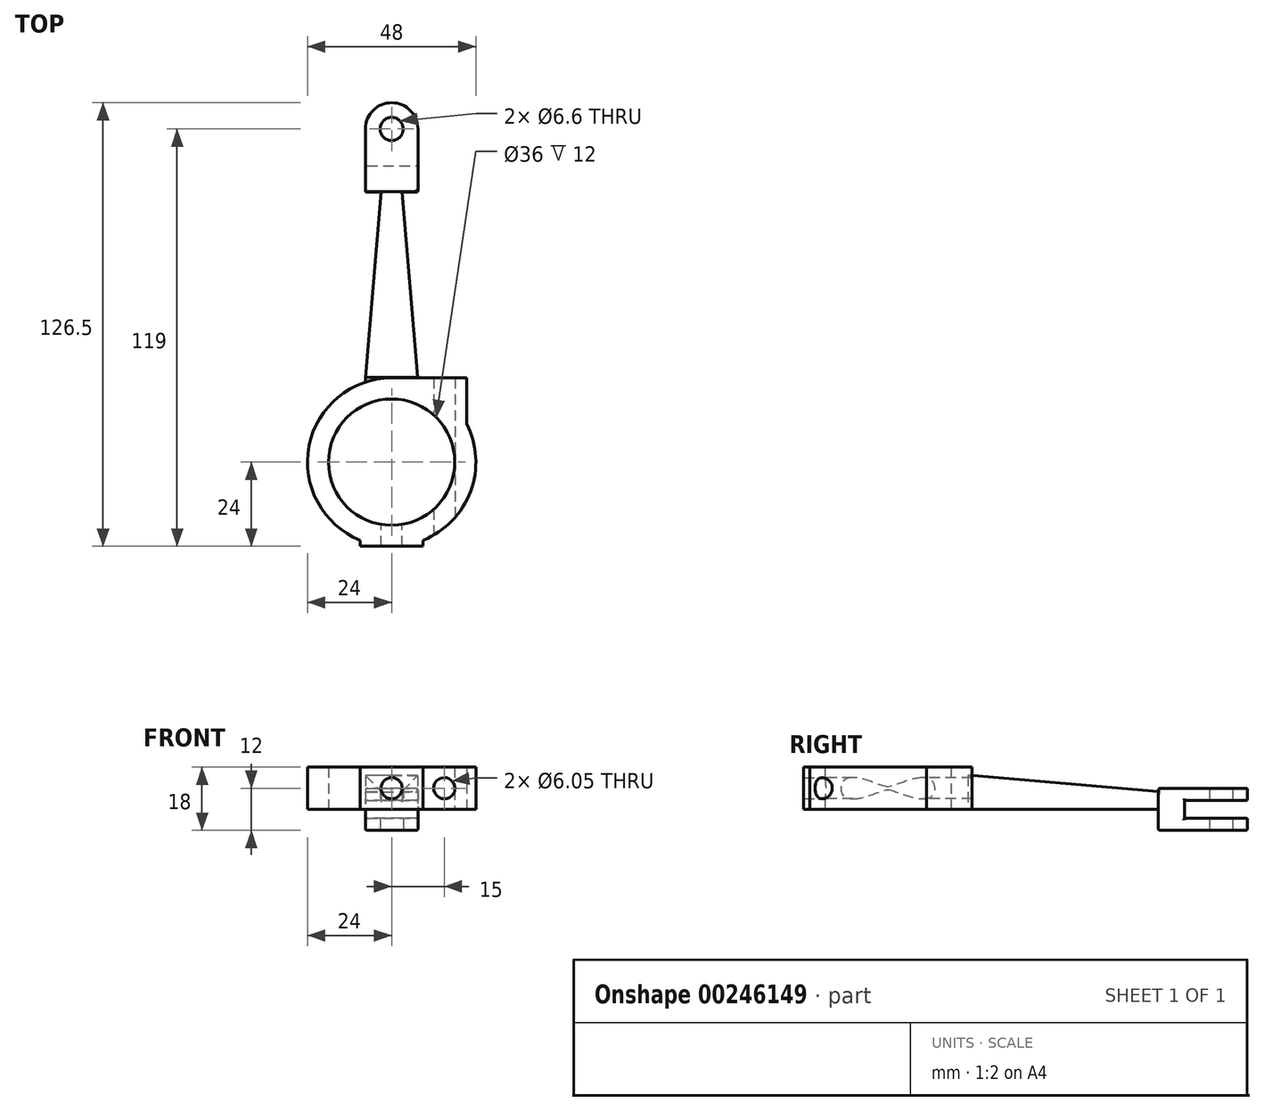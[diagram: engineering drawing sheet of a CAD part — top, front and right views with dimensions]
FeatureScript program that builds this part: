
annotation { "Feature Type Name" : "Feature", "Feature Type Description" : "" }
export const myFeature = defineFeature(function(context is Context, id is Id, definition is map)
    precondition{}
    {
        {
            var Q0;
            Q0=qCreatedBy(makeId("Top.planeOp"),FACE);
            var sketch = newSketch(context, id + "F0", { "sketchPlane" : qUnion([Q0])});
            skCircle(sketch, "E0", {"center": v(0, 0) * mm, "radius": 18 * mm});
            skArc(sketch, "E1", {"start": v(9, -22.25) * mm, "mid": v(22.5, -8.35) * mm, "end": v(21.33, 11) * mm});
            skLineSegment(sketch, "E2", {"start": v(-7.5, 22.8) * mm, "end": v(-3, 77) * mm});
            skLineSegment(sketch, "E3", {"start": v(3, 77) * mm, "end": v(7.4, 24) * mm});
            skLineSegment(sketch, "E4.bottom", {"start": v(-7.5, 95) * mm, "end": v(7.5, 95) * mm, "construction": true});
            skLineSegment(sketch, "E4.left", {"start": v(-7.5, 95) * mm, "end": v(-7.5, 77) * mm});
            skLineSegment(sketch, "E4.right", {"start": v(7.5, 95) * mm, "end": v(7.5, 77) * mm});
            skLineSegment(sketch, "E5", {"start": v(-7.5, 77) * mm, "end": v(-3, 77) * mm});
            skLineSegment(sketch, "E6", {"start": v(3, 77) * mm, "end": v(7.5, 77) * mm});
            skArc(sketch, "E7", {"start": v(7.5, 95) * mm, "mid": v(0, 102.5) * mm, "end": v(-7.5, 95) * mm});
            skCircle(sketch, "E8", {"center": v(0, 95) * mm, "radius": 3.3 * mm});
            skLineSegment(sketch, "E9", {"start": v(0, 24) * mm, "end": v(0, 77) * mm, "construction": true});
            skLineSegment(sketch, "E10", {"start": v(-7.5, 77) * mm, "end": v(7.5, 77) * mm});
            skLineSegment(sketch, "E11", {"start": v(0, 0) * mm, "end": v(0, 95) * mm, "construction": true});
            skLineSegment(sketch, "E12", {"start": v(-9, -22.25) * mm, "end": v(-9, -24) * mm});
            skLineSegment(sketch, "E13", {"start": v(9, -22.25) * mm, "end": v(9, -24) * mm});
            skLineSegment(sketch, "E14", {"start": v(21.33, 11) * mm, "end": v(21.33, 24) * mm});
            skLineSegment(sketch, "E15", {"start": v(21.33, 24) * mm, "end": v(7.4, 24) * mm});
            skLineSegment(sketch, "E16", {"start": v(-9, -24) * mm, "end": v(9, -24) * mm});
            skArc(sketch, "E17.trimOffspring", {"start": v(0, 24) * mm, "mid": v(-23.56, 4.58) * mm, "end": v(-9, -22.25) * mm});
            skLineSegment(sketch, "E18", {"start": v(0, 24) * mm, "end": v(7.4, 24) * mm});
            skSolve(sketch);
        }
        {
            var Q0;
            Q0=makeQuery(id+"F0.imprint","IMPRINT",FACE,{"disambiguationData":[TD([[makeQuery(id+"F0.imprint","IMPRINT",EDGE,{"derivedFrom":sQuery(id+"F0.wireOp",EDGE,"E0")}),-1.0]])]});
            extrude(context, id + "F1", {"entities" : qUnion([Q0]), "depth" : 12 * mm});
        }
        {
            var Q0;
            {var subQ1=sQuery(id+"F0.wireOp",EDGE,"E2");Q0=makeQuery(id+"F0.imprint","IMPRINT",FACE,{"disambiguationData":[TD([[makeQuery(id+"F0.imprint","IMPRINT",EDGE,{"derivedFrom":subQ1}),-1.0]])]});}
            extrude(context, id + "F2", {"entities" : qUnion([Q0]), "operationType" : NewBodyOperationType.ADD, "depth" : 9.6 * mm});
        }
        {
            var Q0;
            {var subQ1=sQuery(id+"F0.wireOp",EDGE,"E4.left");Q0=makeQuery(id+"F0.imprint","IMPRINT",FACE,{"disambiguationData":[TD([[makeQuery(id+"F0.imprint","IMPRINT",EDGE,{"derivedFrom":subQ1}),1.0]])]});}
            extrude(context, id + "F3", {"entities" : qUnion([Q0]), "operationType" : NewBodyOperationType.ADD, "depth" : 6 * mm, "hasSecondDirection" : true, "secondDirectionOppositeDirection" : true, "secondDirectionDepth" : 6 * mm});
        }
        {
            var Q0;
            Q0=qCreatedBy(makeId("Right.planeOp"),FACE);
            var sketch = newSketch(context, id + "F4", { "sketchPlane" : qUnion([Q0])});
            skLineSegment(sketch, "E19", {"start": v(77.12, 5) * mm, "end": v(24.03, 9.61) * mm});
            skLineSegment(sketch, "E20", {"start": v(24.03, 9.61) * mm, "end": v(77.12, 9.61) * mm});
            skLineSegment(sketch, "E21", {"start": v(77.12, 9.61) * mm, "end": v(77.12, 5) * mm});
            skSolve(sketch);
        }
        {
            var Q0;
            Q0 = qSketchRegion(id + "F4", true);
            extrude(context, id + "F5", {"entities" : qUnion([Q0]), "operationType" : NewBodyOperationType.REMOVE, "oppositeDirection" : true, "depth" : 25 * mm, "hasSecondDirection" : true, "secondDirectionOppositeDirection" : false, "secondDirectionDepth" : 25 * mm});
        }
        {
            var Q0;
            Q0=makeQuery(id+"F3.opExtrude","SWEPT_FACE",FACE,{"disambiguationData":[OSD([sQuery(id+"F0.wireOp",EDGE,"E4.right")])]});
            var sketch = newSketch(context, id + "F6", { "sketchPlane" : qUnion([Q0])});
            skLineSegment(sketch, "E22.bottom", {"start": v(102.5, -2.5) * mm, "end": v(84.5, -2.5) * mm});
            skLineSegment(sketch, "E22.top", {"start": v(102.5, 2.5) * mm, "end": v(84.5, 2.5) * mm});
            skLineSegment(sketch, "E22.left", {"start": v(102.5, -2.5) * mm, "end": v(102.5, 2.5) * mm});
            skLineSegment(sketch, "E22.right", {"start": v(84.5, -2.5) * mm, "end": v(84.5, 2.5) * mm});
            skPoint(sketch, "E22.middle", {"position": v(93.5, 0) * mm});
            skSolve(sketch);
        }
        {
            var Q0;
            {var subQ0=sQuery(id+"F6.wireOp",EDGE,"E22.right");Q0=makeQuery(id+"F6.imprint","IMPRINT",FACE,{"disambiguationData":[TD([[makeQuery(id+"F6.imprint","IMPRINT",EDGE,{"derivedFrom":subQ0}),-1.0]])]});}
            var Q1;
            {var subQ0=sQuery(id+"F6.wireOp",EDGE,"E22.left");Q1=makeQuery(id+"F6.imprint","IMPRINT",FACE,{"disambiguationData":[TD([[makeQuery(id+"F6.imprint","IMPRINT",EDGE,{"derivedFrom":subQ0}),1.0]])]});}
            extrude(context, id + "F7", {"entities" : qUnion([Q0, Q1]), "operationType" : NewBodyOperationType.REMOVE, "oppositeDirection" : true, "depth" : 25 * mm});
        }
        {
            var Q0;
            Q0=makeQuery(id+"F1.opExtrude","SWEPT_FACE",FACE,{"disambiguationData":[OSD([sQuery(id+"F0.wireOp",EDGE,"E16")])]});
            var sketch = newSketch(context, id + "F8", { "sketchPlane" : qUnion([Q0])});
            skLineSegment(sketch, "E23", {"start": v(0, 0) * mm, "end": v(0, 12) * mm, "construction": true});
            skLineSegment(sketch, "E24", {"start": v(9, 6) * mm, "end": v(-9, 6) * mm, "construction": true});
            skPoint(sketch, "E25", {"position": v(0, 6) * mm});
            skSolve(sketch);
        }
        {
            var Q0;
            Q0=sQuery(id+"F8.wireOp",VERTEX,"E25");
            var Q1;
            Q1=makeQuery(id+"F1.opExtrude","SWEPT_BODY",BODY,{"disambiguationData":[OSD([sQuery(id+"F0.wireOp",EDGE,"E0"),sQuery(id+"F0.wireOp",EDGE,"E1"),sQuery(id+"F0.wireOp",EDGE,"E12"),sQuery(id+"F0.wireOp",EDGE,"E13"),sQuery(id+"F0.wireOp",EDGE,"E14"),sQuery(id+"F0.wireOp",EDGE,"E15"),sQuery(id+"F0.wireOp",EDGE,"E16"),sQuery(id+"F0.wireOp",EDGE,"E17.trimOffspring"),sQuery(id+"F0.wireOp",EDGE,"E18")])]});
            hole(context, id + "F9", {"style" : HoleStyle.SIMPLE, "endStyle" : HoleEndStyle.BLIND, "holeDiameter" : 5 * mm, "holeDepth" : 17 * mm, "tappedDepth" : 12.7 * mm, "tapClearance" : 3, "locations" : qUnion([Q0]), "scope" : qUnion([Q1]), "startStyle" : HoleStartStyle.PART});
        }
        {
            var Q0;
            Q0=makeQuery(id+"F1.opExtrude","SWEPT_FACE",FACE,{"disambiguationData":[OSD([sQuery(id+"F0.wireOp",EDGE,"E15"),sQuery(id+"F0.wireOp",EDGE,"E18")])]});
            var sketch = newSketch(context, id + "F10", { "sketchPlane" : qUnion([Q0])});
            skLineSegment(sketch, "E26", {"start": v(-21.33, 6) * mm, "end": v(0, 6) * mm, "construction": true});
            skLineSegment(sketch, "E27", {"start": v(-15, 21.84) * mm, "end": v(-15, -13.14) * mm, "construction": true});
            skPoint(sketch, "E28", {"position": v(-15, 6) * mm});
            skSolve(sketch);
        }
        {
            var Q0;
            Q0=sQuery(id+"F10.wireOp",VERTEX,"E28");
            var Q1;
            Q1=makeQuery(id+"F1.opExtrude","SWEPT_BODY",BODY,{"disambiguationData":[OSD([sQuery(id+"F0.wireOp",EDGE,"E0"),sQuery(id+"F0.wireOp",EDGE,"E1"),sQuery(id+"F0.wireOp",EDGE,"E12"),sQuery(id+"F0.wireOp",EDGE,"E13"),sQuery(id+"F0.wireOp",EDGE,"E14"),sQuery(id+"F0.wireOp",EDGE,"E15"),sQuery(id+"F0.wireOp",EDGE,"E16"),sQuery(id+"F0.wireOp",EDGE,"E17.trimOffspring"),sQuery(id+"F0.wireOp",EDGE,"E18")])]});
            hole(context, id + "F11", {"style" : HoleStyle.SIMPLE, "endStyle" : HoleEndStyle.BLIND, "holeDiameter" : 5 * mm, "holeDepth" : 17 * mm, "tappedDepth" : 12.7 * mm, "tapClearance" : 3, "locations" : qUnion([Q0]), "scope" : qUnion([Q1]), "startStyle" : HoleStartStyle.PART});
        }
        {
            var Q0;
            Q0=sQuery(id+"F10.wireOp",VERTEX,"E28");
            var Q1;
            Q1=makeQuery(id+"F1.opExtrude","SWEPT_BODY",BODY,{"disambiguationData":[OSD([sQuery(id+"F0.wireOp",EDGE,"E0"),sQuery(id+"F0.wireOp",EDGE,"E1"),sQuery(id+"F0.wireOp",EDGE,"E12"),sQuery(id+"F0.wireOp",EDGE,"E13"),sQuery(id+"F0.wireOp",EDGE,"E14"),sQuery(id+"F0.wireOp",EDGE,"E15"),sQuery(id+"F0.wireOp",EDGE,"E16"),sQuery(id+"F0.wireOp",EDGE,"E17.trimOffspring"),sQuery(id+"F0.wireOp",EDGE,"E18")])]});
            hole(context, id + "F12", {"style" : HoleStyle.SIMPLE, "endStyle" : HoleEndStyle.BLIND, "holeDiameter" : 6.05 * mm, "holeDepth" : 17 * mm, "tappedDepth" : 12.7 * mm, "tapClearance" : 3, "locations" : qUnion([Q0]), "scope" : qUnion([Q1]), "startStyle" : HoleStartStyle.PART});
        }
        {
            var Q0;
            Q0=sQuery(id+"F8.wireOp",VERTEX,"E25");
            var Q1;
            Q1=makeQuery(id+"F1.opExtrude","SWEPT_BODY",BODY,{"disambiguationData":[OSD([sQuery(id+"F0.wireOp",EDGE,"E0"),sQuery(id+"F0.wireOp",EDGE,"E1"),sQuery(id+"F0.wireOp",EDGE,"E12"),sQuery(id+"F0.wireOp",EDGE,"E13"),sQuery(id+"F0.wireOp",EDGE,"E14"),sQuery(id+"F0.wireOp",EDGE,"E15"),sQuery(id+"F0.wireOp",EDGE,"E16"),sQuery(id+"F0.wireOp",EDGE,"E17.trimOffspring"),sQuery(id+"F0.wireOp",EDGE,"E18")])]});
            hole(context, id + "F13", {"style" : HoleStyle.SIMPLE, "endStyle" : HoleEndStyle.BLIND, "holeDiameter" : 6.05 * mm, "holeDepth" : 17 * mm, "tappedDepth" : 12.7 * mm, "tapClearance" : 3, "locations" : qUnion([Q0]), "scope" : qUnion([Q1]), "startStyle" : HoleStartStyle.PART});
        }
        {
            var Q0;
            Q0=makeQuery(id+"F7.boolean.opBoolean","INTERSECT",EDGE,{"derivedFrom":[makeQuery(id+"F3.opExtrude","SWEPT_FACE",FACE,{"disambiguationData":[OSD([sQuery(id+"F0.wireOp",EDGE,"E7")])]}),makeQuery(id+"F7.opExtrude","SWEPT_FACE",FACE,{"disambiguationData":[OSD([sQuery(id+"F6.wireOp",EDGE,"E22.bottom")])]})]});
            var Q1;
            Q1=makeQuery(id+"F7.boolean.opBoolean","INTERSECT",EDGE,{"derivedFrom":[makeQuery(id+"F3.opExtrude","SWEPT_FACE",FACE,{"disambiguationData":[OSD([sQuery(id+"F0.wireOp",EDGE,"E7")])]}),makeQuery(id+"F7.opExtrude","SWEPT_FACE",FACE,{"disambiguationData":[OSD([sQuery(id+"F6.wireOp",EDGE,"E22.top")])]})]});
            var Q2;
            Q2=makeQuery(id+"F3.opExtrude","CAP_EDGE",EDGE,{"disambiguationData":[OSD([sQuery(id+"F0.wireOp",EDGE,"E7")])],"isStart":false});
            var Q3;
            Q3=makeQuery(id+"F3.opExtrude","CAP_EDGE",EDGE,{"disambiguationData":[OSD([sQuery(id+"F0.wireOp",EDGE,"E7")])],"isStart":true});
            var Q4;
            Q4=makeQuery(id+"F7.boolean.opBoolean","INTERSECT",EDGE,{"derivedFrom":[makeQuery(id+"F3.opExtrude","SWEPT_FACE",FACE,{"disambiguationData":[OSD([sQuery(id+"F0.wireOp",EDGE,"E4.left")])]}),makeQuery(id+"F7.opExtrude","SWEPT_FACE",FACE,{"disambiguationData":[OSD([sQuery(id+"F6.wireOp",EDGE,"E22.right")])]})]});
            var Q5;
            Q5=makeQuery(id+"F3.opExtrude","SWEPT_FACE",FACE,{"disambiguationData":[OSD([sQuery(id+"F0.wireOp",EDGE,"E4.left")])]});
            var Q6;
            Q6=makeQuery(id+"F3.opExtrude","CAP_EDGE",EDGE,{"disambiguationData":[OSD([sQuery(id+"F0.wireOp",EDGE,"E10")])],"isStart":true});
            var Q7;
            Q7=makeQuery(id+"F3.opExtrude","CAP_EDGE",EDGE,{"disambiguationData":[OSD([sQuery(id+"F0.wireOp",EDGE,"E4.right")])],"isStart":true});
            var Q8;
            Q8=makeQuery(id+"F3.opExtrude","SWEPT_EDGE",EDGE,{"disambiguationData":[OSD([sQuery(id+"F0.wireOp",EDGE,"E4.right"),sQuery(id+"F0.wireOp",EDGE,"E10")])]});
            var Q9;
            Q9=makeQuery(id+"F3.opExtrude","CAP_EDGE",EDGE,{"disambiguationData":[OSD([sQuery(id+"F0.wireOp",EDGE,"E4.right")])],"isStart":false});
            var Q10;
            Q10=makeQuery(id+"F7.boolean.opBoolean","COPY",EDGE,{"derivedFrom":makeQuery(id+"F7.opExtrude","CAP_EDGE",EDGE,{"disambiguationData":[OSD([sQuery(id+"F6.wireOp",EDGE,"E22.right")])],"isStart":true})});
            var Q11;
            Q11=makeQuery(id+"F5.boolean.opBoolean","INTERSECT",EDGE,{"derivedFrom":[makeQuery(id+"F3.opExtrude","CAP_FACE",FACE,{"disambiguationData":[OSD([sQuery(id+"F0.wireOp",EDGE,"E4.left"),sQuery(id+"F0.wireOp",EDGE,"E4.right"),sQuery(id+"F0.wireOp",EDGE,"E7"),sQuery(id+"F0.wireOp",EDGE,"E8"),sQuery(id+"F0.wireOp",EDGE,"E10")])],"isStart":false}),makeQuery(id+"F5.opExtrude","SWEPT_FACE",FACE,{"disambiguationData":[OSD([sQuery(id+"F4.wireOp",EDGE,"E21")])]})]});
            fillet(context, id + "F14", {"entities" : qUnion([Q0, Q1, Q2, Q3, Q4, Q5, Q6, Q7, Q8, Q9, Q10, Q11]), "radius" : .5 * mm, "tangentPropagation" : true, "allowEdgeOverflow" : false});
        }
    });
